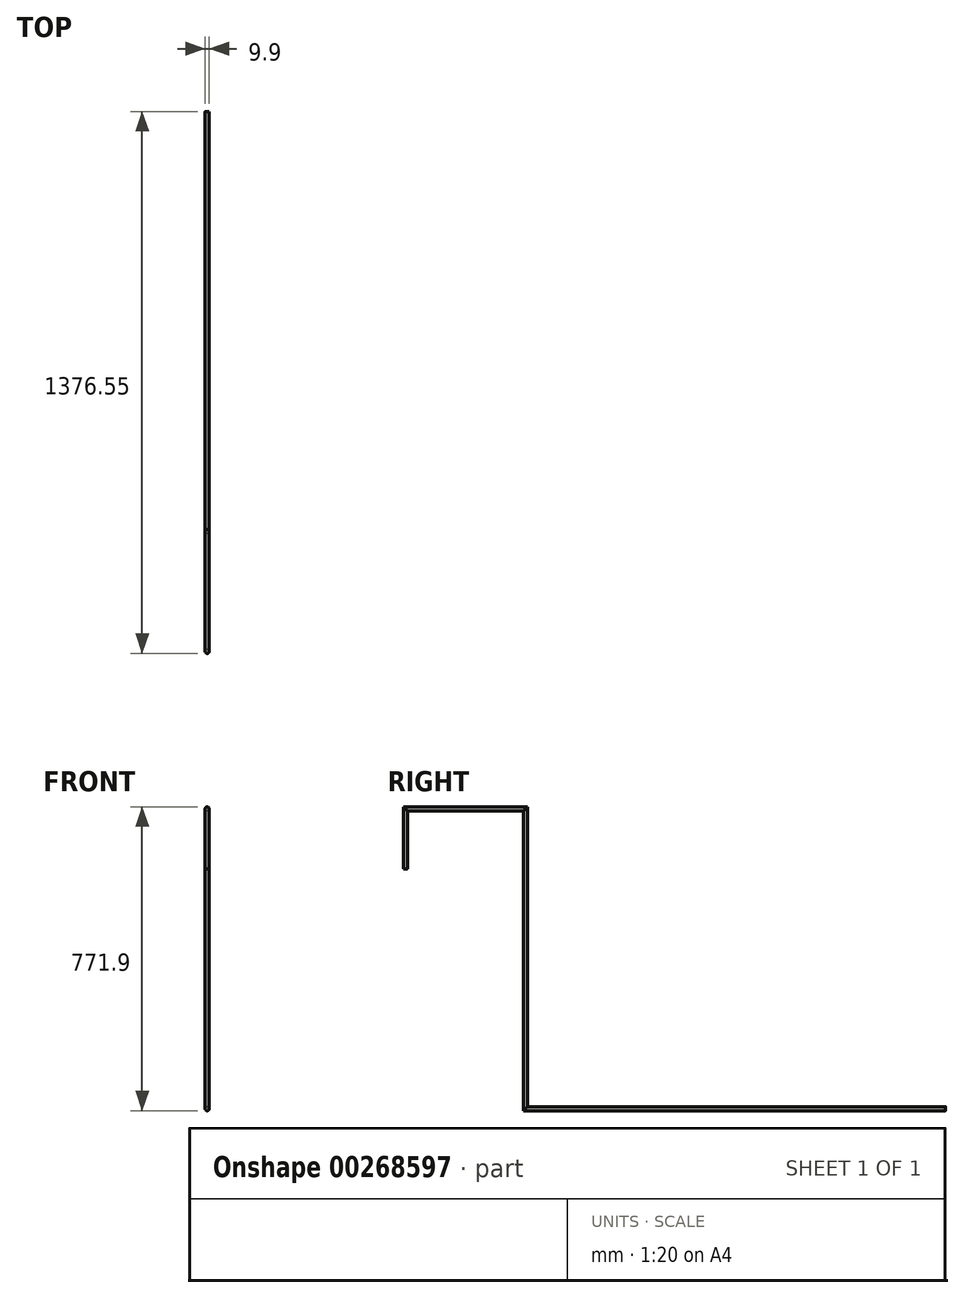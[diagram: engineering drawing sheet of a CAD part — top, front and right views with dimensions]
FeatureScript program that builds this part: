
annotation { "Feature Type Name" : "Feature", "Feature Type Description" : "" }
export const myFeature = defineFeature(function(context is Context, id is Id, definition is map)
    precondition{}
    {
        {
            var Q0;
            Q0=qCreatedBy(makeId("Top.planeOp"),FACE);
            var sketch = newSketch(context, id + "F0", { "sketchPlane" : qUnion([Q0])});
            skCircle(sketch, "E0", {"center": v(0, 0) * mm, "radius": 4.95 * mm});
            skSolve(sketch);
        }
        {
            var Q0;
            Q0=qCreatedBy(makeId("Right.planeOp"),FACE);
            var sketch = newSketch(context, id + "F1", { "sketchPlane" : qUnion([Q0])});
            skLineSegment(sketch, "E1", {"start": v(0, 0) * mm, "end": v(0, 152.4) * mm});
            skLineSegment(sketch, "E2", {"start": v(0, 152.4) * mm, "end": v(304.8, 152.4) * mm});
            skLineSegment(sketch, "E3", {"start": v(304.8, 152.4) * mm, "end": v(304.8, -609.6) * mm});
            skLineSegment(sketch, "E4", {"start": v(304.8, -609.6) * mm, "end": v(1371.6, -609.6) * mm});
            skSolve(sketch);
        }
        {
            var Q0;
            Q0=qSketchRegion(id+"F0",true);
            var Q1;
            Q1=qConstructionFilter(qBodyType(qCreatedBy(id+"F1",EDGE),BodyType.WIRE),ConstructionObject.NO);
            sweep(context, id + "F2", {"profiles" : qUnion([Q0]), "path" : qUnion([Q1])});
        }
    });
